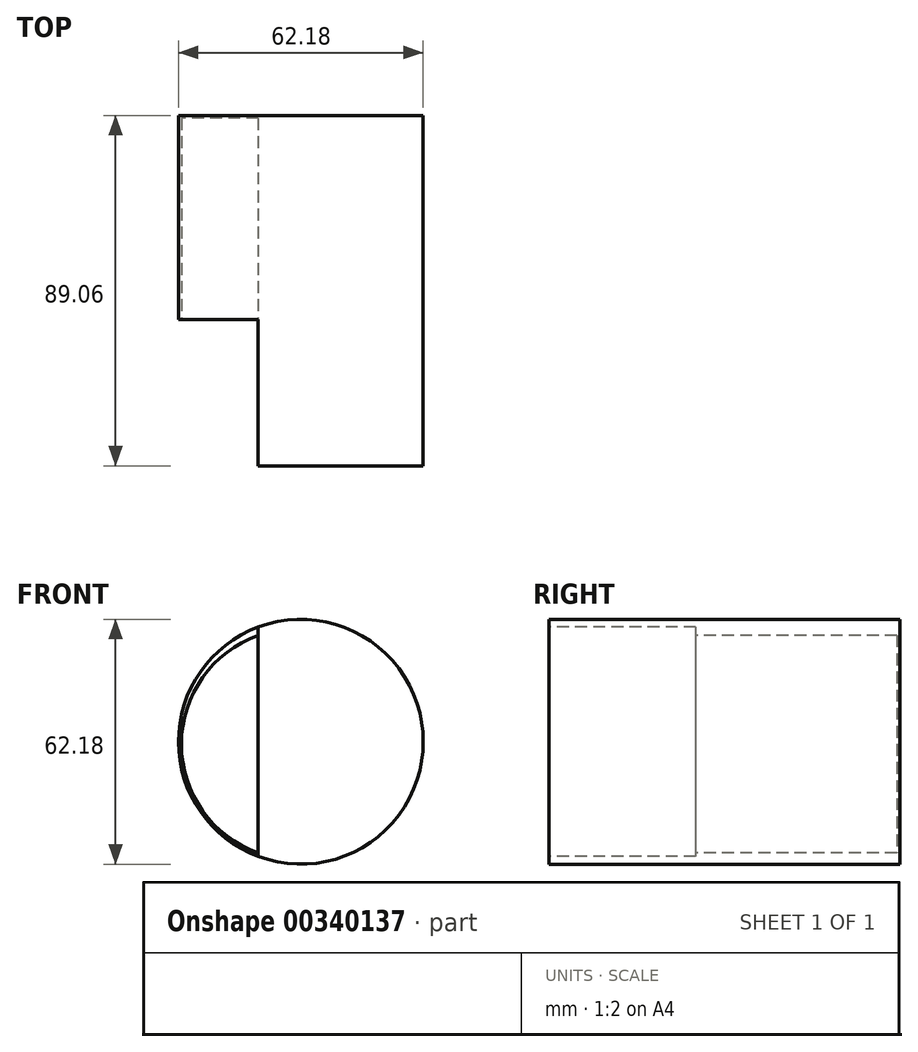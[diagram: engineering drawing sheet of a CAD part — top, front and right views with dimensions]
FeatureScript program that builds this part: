
annotation { "Feature Type Name" : "Feature", "Feature Type Description" : "" }
export const myFeature = defineFeature(function(context is Context, id is Id, definition is map)
    precondition{}
    {
        {
            var Q0;
            Q0=qCreatedBy(makeId("Front.planeOp"),FACE);
            var sketch = newSketch(context, id + "F0", { "sketchPlane" : qUnion([Q0])});
            skCircle(sketch, "E0", {"center": v(0, 0) * mm, "radius": 31.1 * mm});
            skSolve(sketch);
        }
        {
            var Q0;
            Q0=makeQuery(id+"F0.imprint","IMPRINT",FACE,{"disambiguationData":[TD([[makeQuery(id+"F0.imprint","IMPRINT",EDGE,{"derivedFrom":sQuery(id+"F0.wireOp",EDGE,"E0")}),1.0]])]});
            extrude(context, id + "F1", {"entities" : qUnion([Q0]), "depth" : 89.06 * mm});
        }
        {
            var Q0;
            Q0=makeQuery(id+"F1.opExtrude","CAP_FACE",FACE,{"disambiguationData":[OSD([sQuery(id+"F0.wireOp",EDGE,"E0")])],"isStart":false});
            var sketch = newSketch(context, id + "F2", { "sketchPlane" : qUnion([Q0])});
            skLineSegment(sketch, "E1", {"start": v(-10.83, 0) * mm, "end": v(-10.83, 29.15) * mm});
            skLineSegment(sketch, "E2", {"start": v(-10.83, 29.15) * mm, "end": v(-10.83, -29.15) * mm});
            skSolve(sketch);
        }
        {
            var Q0;
            {var subQ0=sQuery(id+"F2.wireOp",EDGE,"E2");var subQ3=makeQuery(id+"F2.imprint","IMPRINT",VERTEX,{"derivedFrom":subQ0});Q0=makeQuery(id+"F2.imprint","IMPRINT",FACE,{"disambiguationData":[TD([[makeQuery(id+"F2.imprint","IMPRINT",EDGE,{"disambiguationData":[TD([[subQ3,1.0]])],"derivedFrom":subQ0}),-1.0]])]});}
            extrude(context, id + "F3", {"entities" : qUnion([Q0]), "operationType" : NewBodyOperationType.REMOVE, "oppositeDirection" : true, "depth" : 37.2 * mm});
        }
        {
            var Q0;
            Q0=makeQuery(id+"F3.boolean.opBoolean","COPY",FACE,{"derivedFrom":makeQuery(id+"F3.opExtrude","CAP_FACE",FACE,{"disambiguationData":[OSD([sQuery(id+"F0.wireOp",EDGE,"E0"),sQuery(id+"F2.wireOp",EDGE,"E2")])],"isStart":false})});
            var sketch = newSketch(context, id + "F4", { "sketchPlane" : qUnion([Q0])});
            skArc(sketch, "E3", {"start": v(-10.83, 27.03) * mm, "mid": v(-30.33, -0.6) * mm, "end": v(-10.83, -28.24) * mm});
            skLineSegment(sketch, "E4", {"start": v(-10.83, 27.03) * mm, "end": v(-10.83, -28.24) * mm});
            skSolve(sketch);
        }
        {
            var Q0;
            Q0 = qSketchRegion(id + "F4", true);
            extrude(context, id + "F5", {"entities" : qUnion([Q0]), "operationType" : NewBodyOperationType.REMOVE, "oppositeDirection" : true, "depth" : 51.14 * mm});
        }
    });
